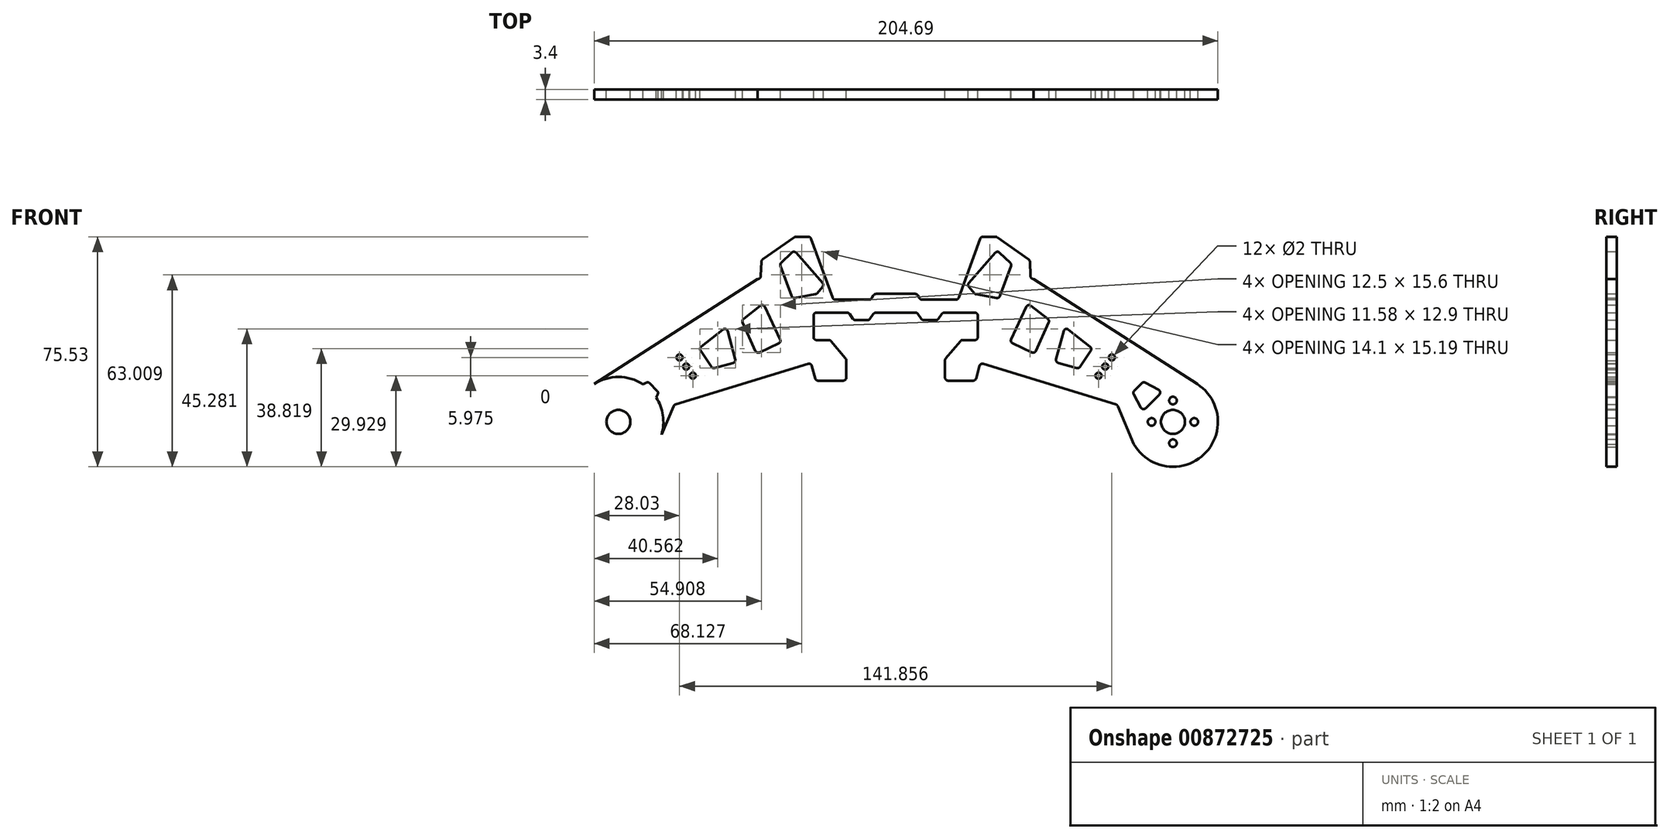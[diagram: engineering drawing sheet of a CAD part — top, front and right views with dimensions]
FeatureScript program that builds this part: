
annotation { "Feature Type Name" : "Feature", "Feature Type Description" : "" }
export const myFeature = defineFeature(function(context is Context, id is Id, definition is map)
    precondition{}
    {
        {
            var Q0;
            Q0=qCreatedBy(makeId("Front.planeOp"),FACE);
            var sketch = newSketch(context, id + "F0", { "sketchPlane" : qUnion([Q0])});
            skLineSegment(sketch, "E0", {"start": v(-61.98, 49.43) * mm, "end": v(-8.3, 14.94) * mm});
            skCircle(sketch, "E1", {"center": v(-16.27, 2.53) * mm, "radius": 14.75 * mm});
            skLineSegment(sketch, "E2", {"start": v(-35, 8.26) * mm, "end": v(-78.52, 21.56) * mm});
            skLineSegment(sketch, "E3", {"start": v(-63, 50.39) * mm, "end": v(-63.19, 55.07) * mm});
            skLineSegment(sketch, "E4", {"start": v(-63.61, 55.85) * mm, "end": v(-74, 63.13) * mm});
            skLineSegment(sketch, "E5", {"start": v(-74.58, 63.31) * mm, "end": v(-78.56, 63.31) * mm});
            skLineSegment(sketch, "E6", {"start": v(-79.5, 62.65) * mm, "end": v(-86.55, 43.3) * mm});
            skLineSegment(sketch, "E7", {"start": v(-87.49, 42.64) * mm, "end": v(-98.58, 42.64) * mm});
            skLineSegment(sketch, "E8", {"start": v(-99.44, 43.14) * mm, "end": v(-99.96, 44.04) * mm});
            skLineSegment(sketch, "E9", {"start": v(-100.83, 44.54) * mm, "end": v(-107.25, 44.54) * mm});
            skLineSegment(sketch, "E10", {"start": v(-79.77, 20.86) * mm, "end": v(-80.86, 16.81) * mm});
            skLineSegment(sketch, "E11", {"start": v(-81.83, 16.07) * mm, "end": v(-90.06, 16.07) * mm});
            skLineSegment(sketch, "E12", {"start": v(-91.06, 17.07) * mm, "end": v(-91.06, 22.7) * mm});
            skLineSegment(sketch, "E13", {"start": v(-90.83, 23.35) * mm, "end": v(-86.06, 29.03) * mm});
            skLineSegment(sketch, "E14", {"start": v(-85.3, 29.39) * mm, "end": v(-81.3, 29.39) * mm});
            skLineSegment(sketch, "E15", {"start": v(-80.3, 30.39) * mm, "end": v(-80.3, 37.39) * mm});
            skLineSegment(sketch, "E16", {"start": v(-81.3, 38.39) * mm, "end": v(-91.3, 38.39) * mm});
            skLineSegment(sketch, "E17", {"start": v(-92.1, 37.96) * mm, "end": v(-93.23, 36.36) * mm});
            skLineSegment(sketch, "E18", {"start": v(-94.05, 35.93) * mm, "end": v(-98.01, 35.93) * mm});
            skLineSegment(sketch, "E19", {"start": v(-98.83, 36.36) * mm, "end": v(-99.95, 37.96) * mm});
            skLineSegment(sketch, "E20", {"start": v(-100.77, 38.39) * mm, "end": v(-107.25, 38.39) * mm});
            skLineSegment(sketch, "E21", {"start": v(-34.38, 7.7) * mm, "end": v(-29.1, -4.76) * mm});
            skCircle(sketch, "E22", {"center": v(-16.27, 2.53) * mm, "radius": 3.93 * mm});
            skLineSegment(sketch, "E23", {"start": v(-16.27, 2.53) * mm, "end": v(-16.27, 9.53) * mm, "construction": true});
            skLineSegment(sketch, "E24", {"start": v(-16.27, 2.53) * mm, "end": v(-9.27, 2.53) * mm, "construction": true});
            skLineSegment(sketch, "E25", {"start": v(-16.27, 2.53) * mm, "end": v(-23.27, 2.53) * mm, "construction": true});
            skLineSegment(sketch, "E26", {"start": v(-16.27, 2.53) * mm, "end": v(-16.27, -4.47) * mm, "construction": true});
            skCircle(sketch, "E27", {"center": v(-16.27, -4.47) * mm, "radius": 1.25 * mm});
            skCircle(sketch, "E28", {"center": v(-9.27, 2.53) * mm, "radius": 1.25 * mm});
            skCircle(sketch, "E29", {"center": v(-16.27, 9.53) * mm, "radius": 1.25 * mm});
            skCircle(sketch, "E30", {"center": v(-23.27, 2.53) * mm, "radius": 1.25 * mm});
            skLineSegment(sketch, "E31", {"start": v(-25.22, 7.02) * mm, "end": v(-20.75, 11.48) * mm});
            skLineSegment(sketch, "E32", {"start": v(-20.99, 13.07) * mm, "end": v(-25.3, 15.4) * mm});
            skLineSegment(sketch, "E33", {"start": v(-26.5, 15.23) * mm, "end": v(-28.97, 12.75) * mm});
            skLineSegment(sketch, "E34", {"start": v(-29.14, 11.57) * mm, "end": v(-26.8, 7.25) * mm});
            skPoint(sketch, "E35", {"position": v(-22.99, 9.25) * mm});
            skCircle(sketch, "E36", {"center": v(-40.68, 17.7) * mm, "radius": 1 * mm});
            skCircle(sketch, "E37", {"center": v(-38.5, 20.7) * mm, "radius": 1 * mm});
            skCircle(sketch, "E38", {"center": v(-36.32, 23.68) * mm, "radius": 1 * mm});
            skLineSegment(sketch, "E39", {"start": v(-38.5, 20.7) * mm, "end": v(-40.68, 17.7) * mm, "construction": true});
            skLineSegment(sketch, "E40", {"start": v(-36.32, 23.68) * mm, "end": v(-38.5, 20.7) * mm, "construction": true});
            skLineSegment(sketch, "E41", {"start": v(-46.77, 20.6) * mm, "end": v(-43.24, 25.86) * mm});
            skLineSegment(sketch, "E42", {"start": v(-43.45, 27.2) * mm, "end": v(-50.54, 32.83) * mm});
            skLineSegment(sketch, "E43", {"start": v(-52.13, 32.31) * mm, "end": v(-54.61, 23.14) * mm});
            skLineSegment(sketch, "E44", {"start": v(-53.92, 21.92) * mm, "end": v(-47.88, 20.19) * mm});
            skPoint(sketch, "E45", {"position": v(-44.95, 23.3) * mm});
            skPoint(sketch, "E46.endSnap0", {"position": v(-57.03, 15) * mm});
            skLineSegment(sketch, "E47", {"start": v(-62.54, 25.36) * mm, "end": v(-68.87, 28.3) * mm});
            skLineSegment(sketch, "E48", {"start": v(-69.36, 29.64) * mm, "end": v(-64.4, 40.28) * mm});
            skLineSegment(sketch, "E49", {"start": v(-62.87, 40.65) * mm, "end": v(-57.34, 36.36) * mm});
            skLineSegment(sketch, "E50", {"start": v(-57.04, 35.16) * mm, "end": v(-61.2, 25.85) * mm});
            skPoint(sketch, "E51.visualSharp", {"position": v(-63.86, 41.42) * mm});
            skArc(sketch, "E51.filletArc", {"start": v(-62.87, 40.65) * mm, "mid": v(-63.72, 40.83) * mm, "end": v(-64.4, 40.28) * mm});
            skPoint(sketch, "E52.visualSharp", {"position": v(-56.72, 35.88) * mm});
            skArc(sketch, "E52.filletArc", {"start": v(-57.04, 35.16) * mm, "mid": v(-56.98, 35.81) * mm, "end": v(-57.34, 36.36) * mm});
            skPoint(sketch, "E53.visualSharp", {"position": v(-69.78, 28.73) * mm});
            skArc(sketch, "E53.filletArc", {"start": v(-69.36, 29.64) * mm, "mid": v(-69.4, 28.87) * mm, "end": v(-68.87, 28.3) * mm});
            skPoint(sketch, "E54.visualSharp", {"position": v(-61.62, 24.93) * mm});
            skArc(sketch, "E54.filletArc", {"start": v(-62.54, 25.36) * mm, "mid": v(-61.77, 25.32) * mm, "end": v(-61.2, 25.85) * mm});
            skPoint(sketch, "E55.visualSharp", {"position": v(-51.73, 33.78) * mm});
            skArc(sketch, "E55.filletArc", {"start": v(-50.54, 32.83) * mm, "mid": v(-51.48, 33) * mm, "end": v(-52.13, 32.31) * mm});
            skPoint(sketch, "E56.visualSharp", {"position": v(-42.72, 26.63) * mm});
            skArc(sketch, "E56.filletArc", {"start": v(-43.24, 25.86) * mm, "mid": v(-43.08, 26.58) * mm, "end": v(-43.45, 27.2) * mm});
            skPoint(sketch, "E57.visualSharp", {"position": v(-54.87, 22.2) * mm});
            skArc(sketch, "E57.filletArc", {"start": v(-54.61, 23.14) * mm, "mid": v(-54.52, 22.4) * mm, "end": v(-53.92, 21.92) * mm});
            skPoint(sketch, "E58.visualSharp", {"position": v(-47.18, 19.99) * mm});
            skArc(sketch, "E58.filletArc", {"start": v(-47.88, 20.19) * mm, "mid": v(-47.26, 20.21) * mm, "end": v(-46.77, 20.6) * mm});
            skPoint(sketch, "E59.visualSharp", {"position": v(-29.5, 12.22) * mm});
            skArc(sketch, "E59.filletArc", {"start": v(-28.97, 12.75) * mm, "mid": v(-29.25, 12.19) * mm, "end": v(-29.14, 11.57) * mm});
            skPoint(sketch, "E60.visualSharp", {"position": v(-25.96, 15.76) * mm});
            skArc(sketch, "E60.filletArc", {"start": v(-25.3, 15.4) * mm, "mid": v(-25.93, 15.52) * mm, "end": v(-26.5, 15.23) * mm});
            skPoint(sketch, "E61.visualSharp", {"position": v(-26.17, 6.07) * mm});
            skArc(sketch, "E61.filletArc", {"start": v(-26.8, 7.25) * mm, "mid": v(-26.07, 6.73) * mm, "end": v(-25.22, 7.02) * mm});
            skPoint(sketch, "E62.visualSharp", {"position": v(-19.8, 12.43) * mm});
            skArc(sketch, "E62.filletArc", {"start": v(-20.75, 11.48) * mm, "mid": v(-20.47, 12.33) * mm, "end": v(-20.99, 13.07) * mm});
            skPoint(sketch, "E63.visualSharp", {"position": v(-62.99, 50.07) * mm});
            skArc(sketch, "E63.filletArc", {"start": v(-63, 50.39) * mm, "mid": v(-62.68, 49.7) * mm, "end": v(-61.98, 49.43) * mm});
            skPoint(sketch, "E64.visualSharp", {"position": v(-63.2, 55.57) * mm});
            skArc(sketch, "E64.filletArc", {"start": v(-63.19, 55.07) * mm, "mid": v(-63.3, 55.51) * mm, "end": v(-63.61, 55.85) * mm});
            skPoint(sketch, "E65.visualSharp", {"position": v(-100.25, 38.39) * mm});
            skArc(sketch, "E65.filletArc", {"start": v(-99.95, 37.96) * mm, "mid": v(-100.31, 38.28) * mm, "end": v(-100.77, 38.39) * mm});
            skPoint(sketch, "E66.visualSharp", {"position": v(-98.53, 35.93) * mm});
            skArc(sketch, "E66.filletArc", {"start": v(-98.83, 36.36) * mm, "mid": v(-98.47, 36.04) * mm, "end": v(-98.01, 35.93) * mm});
            skPoint(sketch, "E67.visualSharp", {"position": v(-93.53, 35.93) * mm});
            skArc(sketch, "E67.filletArc", {"start": v(-94.05, 35.93) * mm, "mid": v(-93.6, 36.04) * mm, "end": v(-93.23, 36.36) * mm});
            skPoint(sketch, "E68.visualSharp", {"position": v(-91.81, 38.39) * mm});
            skArc(sketch, "E68.filletArc", {"start": v(-91.3, 38.39) * mm, "mid": v(-91.75, 38.28) * mm, "end": v(-92.1, 37.96) * mm});
            skPoint(sketch, "E69.visualSharp", {"position": v(-80.3, 38.39) * mm});
            skArc(sketch, "E69.filletArc", {"start": v(-80.3, 37.39) * mm, "mid": v(-80.58, 38.1) * mm, "end": v(-81.3, 38.39) * mm});
            skPoint(sketch, "E70.visualSharp", {"position": v(-80.3, 29.39) * mm});
            skArc(sketch, "E70.filletArc", {"start": v(-81.3, 29.39) * mm, "mid": v(-80.58, 29.68) * mm, "end": v(-80.3, 30.39) * mm});
            skPoint(sketch, "E71.visualSharp", {"position": v(-85.76, 29.39) * mm});
            skArc(sketch, "E71.filletArc", {"start": v(-85.3, 29.39) * mm, "mid": v(-85.71, 29.3) * mm, "end": v(-86.06, 29.03) * mm});
            skPoint(sketch, "E72.visualSharp", {"position": v(-91.06, 23.07) * mm});
            skArc(sketch, "E72.filletArc", {"start": v(-90.83, 23.35) * mm, "mid": v(-91, 23.05) * mm, "end": v(-91.06, 22.7) * mm});
            skPoint(sketch, "E73.visualSharp", {"position": v(-91.06, 16.07) * mm});
            skArc(sketch, "E73.filletArc", {"start": v(-91.06, 17.07) * mm, "mid": v(-90.77, 16.36) * mm, "end": v(-90.06, 16.07) * mm});
            skPoint(sketch, "E74.visualSharp", {"position": v(-81.06, 16.07) * mm});
            skArc(sketch, "E74.filletArc", {"start": v(-81.83, 16.07) * mm, "mid": v(-81.22, 16.28) * mm, "end": v(-80.86, 16.81) * mm});
            skPoint(sketch, "E75.visualSharp", {"position": v(-79.5, 21.87) * mm});
            skArc(sketch, "E75.filletArc", {"start": v(-78.52, 21.56) * mm, "mid": v(-79.3, 21.48) * mm, "end": v(-79.77, 20.86) * mm});
            skPoint(sketch, "E76.visualSharp", {"position": v(-86.79, 42.64) * mm});
            skArc(sketch, "E76.filletArc", {"start": v(-87.49, 42.64) * mm, "mid": v(-86.91, 42.82) * mm, "end": v(-86.55, 43.3) * mm});
            skPoint(sketch, "E77.visualSharp", {"position": v(-34.56, 8.12) * mm});
            skArc(sketch, "E77.filletArc", {"start": v(-34.38, 7.7) * mm, "mid": v(-34.63, 8.05) * mm, "end": v(-35, 8.26) * mm});
            skPoint(sketch, "E78.visualSharp", {"position": v(-79.26, 63.31) * mm});
            skArc(sketch, "E78.filletArc", {"start": v(-78.56, 63.31) * mm, "mid": v(-79.14, 63.13) * mm, "end": v(-79.5, 62.65) * mm});
            skPoint(sketch, "E79.visualSharp", {"position": v(-74.26, 63.31) * mm});
            skArc(sketch, "E79.filletArc", {"start": v(-74, 63.13) * mm, "mid": v(-74.28, 63.27) * mm, "end": v(-74.58, 63.31) * mm});
            skLineSegment(sketch, "E80.MirrorCS", {"start": v(-74.58, 58.04) * mm, "end": v(-83.22, 48.2) * mm});
            skLineSegment(sketch, "E81.MirrorCS", {"start": v(-69.68, 54.77) * mm, "end": v(-73.13, 58.1) * mm});
            skLineSegment(sketch, "E82.MirrorCS", {"start": v(-80.87, 44.42) * mm, "end": v(-74.18, 43.21) * mm});
            skLineSegment(sketch, "E83.MirrorCS", {"start": v(-73.07, 43.85) * mm, "end": v(-69.43, 53.7) * mm});
            skLineSegment(sketch, "E84.MirrorCS", {"start": v(-83.24, 46.9) * mm, "end": v(-81.46, 44.77) * mm});
            skPoint(sketch, "E85.MirrorP", {"position": v(-86.1, 45.52) * mm});
            skPoint(sketch, "E86.visualSharp", {"position": v(-73.89, 58.83) * mm});
            skArc(sketch, "E86.filletArc", {"start": v(-73.13, 58.1) * mm, "mid": v(-73.87, 58.38) * mm, "end": v(-74.58, 58.04) * mm});
            skPoint(sketch, "E87.visualSharp", {"position": v(-69.2, 54.32) * mm});
            skArc(sketch, "E87.filletArc", {"start": v(-69.43, 53.7) * mm, "mid": v(-69.4, 54.28) * mm, "end": v(-69.68, 54.77) * mm});
            skPoint(sketch, "E88.visualSharp", {"position": v(-73.36, 43.06) * mm});
            skArc(sketch, "E88.filletArc", {"start": v(-74.18, 43.21) * mm, "mid": v(-73.5, 43.33) * mm, "end": v(-73.07, 43.85) * mm});
            skPoint(sketch, "E89.visualSharp", {"position": v(-81.23, 44.49) * mm});
            skArc(sketch, "E89.filletArc", {"start": v(-81.46, 44.77) * mm, "mid": v(-81.2, 44.54) * mm, "end": v(-80.87, 44.42) * mm});
            skPoint(sketch, "E90.visualSharp", {"position": v(-83.79, 47.56) * mm});
            skArc(sketch, "E90.filletArc", {"start": v(-83.22, 48.2) * mm, "mid": v(-83.47, 47.56) * mm, "end": v(-83.24, 46.9) * mm});
            skLineSegment(sketch, "E91", {"start": v(-36.32, 23.68) * mm, "end": v(-31.73, 30) * mm, "construction": true});
            skLineSegment(sketch, "E92", {"start": v(-40.68, 17.7) * mm, "end": v(-45.28, 11.4) * mm, "construction": true});
            skLineSegment(sketch, "E93", {"start": v(-16.27, 2.53) * mm, "end": v(-22.99, 9.25) * mm, "construction": true});
            skLineSegment(sketch, "E94", {"start": v(-47.18, 19.99) * mm, "end": v(-51.64, 13.34) * mm, "construction": true});
            skPoint(sketch, "E95.endSnap0", {"position": v(-35.14, 32.18) * mm});
            skLineSegment(sketch, "E96", {"start": v(-64.55, 26.29) * mm, "end": v(-67.4, 18.16) * mm, "construction": true});
            skLineSegment(sketch, "E97", {"start": v(-54.87, 22.2) * mm, "end": v(-56.82, 15) * mm, "construction": true});
            skLineSegment(sketch, "E98", {"start": v(-42.72, 26.63) * mm, "end": v(-37.84, 33.92) * mm, "construction": true});
            skLineSegment(sketch, "E99", {"start": v(-51.73, 33.78) * mm, "end": v(-49.64, 41.5) * mm, "construction": true});
            skPoint(sketch, "E100.visualSharp", {"position": v(-100.25, 44.54) * mm});
            skArc(sketch, "E100.filletArc", {"start": v(-99.96, 44.04) * mm, "mid": v(-100.33, 44.4) * mm, "end": v(-100.83, 44.54) * mm});
            skPoint(sketch, "E101.visualSharp", {"position": v(-99.16, 42.64) * mm});
            skArc(sketch, "E101.filletArc", {"start": v(-99.44, 43.14) * mm, "mid": v(-99.08, 42.77) * mm, "end": v(-98.58, 42.64) * mm});
            skLineSegment(sketch, "E102.MirrorCS", {"start": v(-180.13, 7.7) * mm, "end": v(-185.41, -4.76) * mm});
            skCircle(sketch, "E103.MirrorC", {"center": v(-198.23, 2.53) * mm, "radius": 3.93 * mm});
            skLineSegment(sketch, "E104.MirrorCS", {"start": v(-198.23, 2.53) * mm, "end": v(-198.23, -4.47) * mm, "construction": true});
            skCircle(sketch, "E105.MirrorC", {"center": v(-198.23, 2.53) * mm, "radius": 14.75 * mm});
            skArc(sketch, "E106.MirrorCS", {"start": v(-120.45, 35.93) * mm, "mid": v(-120.91, 36.04) * mm, "end": v(-121.27, 36.36) * mm});
            skLineSegment(sketch, "E107.MirrorCS", {"start": v(-122.4, 37.96) * mm, "end": v(-121.27, 36.36) * mm});
            skArc(sketch, "E108.MirrorCS", {"start": v(-123.21, 38.39) * mm, "mid": v(-122.75, 38.28) * mm, "end": v(-122.4, 37.96) * mm});
            skArc(sketch, "E109.MirrorCS", {"start": v(-180.13, 7.7) * mm, "mid": v(-179.88, 8.05) * mm, "end": v(-179.5, 8.26) * mm});
            skArc(sketch, "E110.MirrorCS", {"start": v(-140.5, 63.13) * mm, "mid": v(-140.23, 63.27) * mm, "end": v(-139.93, 63.31) * mm});
            skArc(sketch, "E111.MirrorCS", {"start": v(-115.06, 43.14) * mm, "mid": v(-115.43, 42.77) * mm, "end": v(-115.93, 42.64) * mm});
            skLineSegment(sketch, "E112.MirrorCS", {"start": v(-178.18, 23.68) * mm, "end": v(-176, 20.7) * mm, "construction": true});
            skCircle(sketch, "E113.MirrorC", {"center": v(-178.18, 23.68) * mm, "radius": 1 * mm});
            skLineSegment(sketch, "E114.MirrorCS", {"start": v(-188.01, 15.23) * mm, "end": v(-185.53, 12.75) * mm});
            skArc(sketch, "E115.MirrorCS", {"start": v(-114.55, 37.96) * mm, "mid": v(-114.2, 38.28) * mm, "end": v(-113.73, 38.39) * mm});
            skArc(sketch, "E116.MirrorCS", {"start": v(-133.21, 29.39) * mm, "mid": v(-133.92, 29.68) * mm, "end": v(-134.21, 30.39) * mm});
            skArc(sketch, "E117.MirrorCS", {"start": v(-133.04, 44.77) * mm, "mid": v(-133.3, 44.54) * mm, "end": v(-133.63, 44.42) * mm});
            skArc(sketch, "E118.MirrorCS", {"start": v(-193.75, 11.48) * mm, "mid": v(-194.03, 12.33) * mm, "end": v(-193.52, 13.07) * mm});
            skLineSegment(sketch, "E119.MirrorCS", {"start": v(-131.26, 46.9) * mm, "end": v(-133.04, 44.77) * mm});
            skArc(sketch, "E120.MirrorCS", {"start": v(-135.99, 21.56) * mm, "mid": v(-135.21, 21.48) * mm, "end": v(-134.73, 20.86) * mm});
            skLineSegment(sketch, "E121.MirrorCS", {"start": v(-176, 20.7) * mm, "end": v(-173.82, 17.7) * mm, "construction": true});
            skLineSegment(sketch, "E122.MirrorCS", {"start": v(-115.67, 36.36) * mm, "end": v(-114.55, 37.96) * mm});
            skArc(sketch, "E123.MirrorCS", {"start": v(-151.63, 40.65) * mm, "mid": v(-150.78, 40.83) * mm, "end": v(-150.11, 40.28) * mm});
            skArc(sketch, "E124.MirrorCS", {"start": v(-145.07, 53.7) * mm, "mid": v(-145.1, 54.28) * mm, "end": v(-144.83, 54.77) * mm});
            skCircle(sketch, "E125.MirrorC", {"center": v(-173.82, 17.7) * mm, "radius": 1 * mm});
            skLineSegment(sketch, "E126.MirrorCS", {"start": v(-129.21, 29.39) * mm, "end": v(-133.21, 29.39) * mm});
            skCircle(sketch, "E127.MirrorC", {"center": v(-176, 20.7) * mm, "radius": 1 * mm});
            skArc(sketch, "E128.MirrorCS", {"start": v(-115.67, 36.36) * mm, "mid": v(-116.03, 36.04) * mm, "end": v(-116.5, 35.93) * mm});
            skArc(sketch, "E129.MirrorCS", {"start": v(-123.68, 23.35) * mm, "mid": v(-123.5, 23.05) * mm, "end": v(-123.44, 22.7) * mm});
            skLineSegment(sketch, "E130.MirrorCS", {"start": v(-115.06, 43.14) * mm, "end": v(-114.54, 44.04) * mm});
            skArc(sketch, "E131.MirrorCS", {"start": v(-127.02, 42.64) * mm, "mid": v(-127.59, 42.82) * mm, "end": v(-127.96, 43.3) * mm});
            skArc(sketch, "E132.MirrorCS", {"start": v(-132.68, 16.07) * mm, "mid": v(-133.29, 16.28) * mm, "end": v(-133.64, 16.81) * mm});
            skArc(sketch, "E133.MirrorCS", {"start": v(-131.28, 48.2) * mm, "mid": v(-131.03, 47.56) * mm, "end": v(-131.26, 46.9) * mm});
            skLineSegment(sketch, "E134.MirrorCS", {"start": v(-134.73, 20.86) * mm, "end": v(-133.64, 16.81) * mm});
            skLineSegment(sketch, "E135.MirrorCS", {"start": v(-120.45, 35.93) * mm, "end": v(-116.5, 35.93) * mm});
            skArc(sketch, "E136.MirrorCS", {"start": v(-189.2, 15.4) * mm, "mid": v(-188.58, 15.52) * mm, "end": v(-188.01, 15.23) * mm});
            skArc(sketch, "E137.MirrorCS", {"start": v(-151.32, 55.07) * mm, "mid": v(-151.2, 55.51) * mm, "end": v(-150.9, 55.85) * mm});
            skArc(sketch, "E138.MirrorCS", {"start": v(-129.21, 29.39) * mm, "mid": v(-128.8, 29.3) * mm, "end": v(-128.45, 29.03) * mm});
            skArc(sketch, "E139.MirrorCS", {"start": v(-114.54, 44.04) * mm, "mid": v(-114.17, 44.4) * mm, "end": v(-113.67, 44.54) * mm});
            skLineSegment(sketch, "E140.MirrorCS", {"start": v(-144.83, 54.77) * mm, "end": v(-141.37, 58.1) * mm});
            skArc(sketch, "E141.MirrorCS", {"start": v(-166.63, 20.19) * mm, "mid": v(-167.24, 20.21) * mm, "end": v(-167.73, 20.6) * mm});
            skArc(sketch, "E142.MirrorCS", {"start": v(-141.37, 58.1) * mm, "mid": v(-140.64, 58.38) * mm, "end": v(-139.93, 58.04) * mm});
            skArc(sketch, "E143.MirrorCS", {"start": v(-185.53, 12.75) * mm, "mid": v(-185.25, 12.19) * mm, "end": v(-185.36, 11.57) * mm});
            skLineSegment(sketch, "E144.MirrorCS", {"start": v(-113.73, 38.39) * mm, "end": v(-107.25, 38.39) * mm});
            skCircle(sketch, "E145.MirrorC", {"center": v(-198.23, -4.47) * mm, "radius": 1.25 * mm});
            skCircle(sketch, "E146.MirrorC", {"center": v(-198.23, 9.53) * mm, "radius": 1.25 * mm});
            skArc(sketch, "E147.MirrorCS", {"start": v(-145.15, 29.64) * mm, "mid": v(-145.11, 28.87) * mm, "end": v(-145.63, 28.3) * mm});
            skArc(sketch, "E148.MirrorCS", {"start": v(-134.21, 37.39) * mm, "mid": v(-133.92, 38.1) * mm, "end": v(-133.21, 38.39) * mm});
            skArc(sketch, "E149.MirrorCS", {"start": v(-157.47, 35.16) * mm, "mid": v(-157.52, 35.81) * mm, "end": v(-157.17, 36.36) * mm});
            skArc(sketch, "E150.MirrorCS", {"start": v(-163.96, 32.83) * mm, "mid": v(-163.03, 33) * mm, "end": v(-162.37, 32.31) * mm});
            skArc(sketch, "E151.MirrorCS", {"start": v(-171.27, 25.86) * mm, "mid": v(-171.42, 26.58) * mm, "end": v(-171.06, 27.2) * mm});
            skLineSegment(sketch, "E152.MirrorCS", {"start": v(-113.67, 44.54) * mm, "end": v(-107.25, 44.54) * mm});
            skLineSegment(sketch, "E153.MirrorCS", {"start": v(-193.52, 13.07) * mm, "end": v(-189.2, 15.4) * mm});
            skCircle(sketch, "E154.MirrorC", {"center": v(-205.23, 2.53) * mm, "radius": 1.25 * mm});
            skArc(sketch, "E155.MirrorCS", {"start": v(-187.7, 7.25) * mm, "mid": v(-188.43, 6.73) * mm, "end": v(-189.28, 7.02) * mm});
            skArc(sketch, "E156.MirrorCS", {"start": v(-123.44, 17.07) * mm, "mid": v(-123.74, 16.36) * mm, "end": v(-124.44, 16.07) * mm});
            skLineSegment(sketch, "E157.MirrorCS", {"start": v(-167.73, 20.6) * mm, "end": v(-171.27, 25.86) * mm});
            skArc(sketch, "E158.MirrorCS", {"start": v(-140.32, 43.21) * mm, "mid": v(-141, 43.33) * mm, "end": v(-141.44, 43.85) * mm});
            skCircle(sketch, "E159.MirrorC", {"center": v(-191.23, 2.53) * mm, "radius": 1.25 * mm});
            skLineSegment(sketch, "E160.MirrorCS", {"start": v(-139.93, 63.31) * mm, "end": v(-135.94, 63.31) * mm});
            skArc(sketch, "E161.MirrorCS", {"start": v(-135.94, 63.31) * mm, "mid": v(-135.37, 63.13) * mm, "end": v(-135, 62.65) * mm});
            skArc(sketch, "E162.MirrorCS", {"start": v(-159.9, 23.14) * mm, "mid": v(-159.99, 22.4) * mm, "end": v(-160.58, 21.92) * mm});
            skLineSegment(sketch, "E163.MirrorCS", {"start": v(-185.36, 11.57) * mm, "end": v(-187.7, 7.25) * mm});
            skLineSegment(sketch, "E164.MirrorCS", {"start": v(-189.28, 7.02) * mm, "end": v(-193.75, 11.48) * mm});
            skArc(sketch, "E165.MirrorCS", {"start": v(-151.96, 25.36) * mm, "mid": v(-152.73, 25.32) * mm, "end": v(-153.3, 25.85) * mm});
            skLineSegment(sketch, "E166.MirrorCS", {"start": v(-151.5, 50.39) * mm, "end": v(-151.32, 55.07) * mm});
            skArc(sketch, "E167.MirrorCS", {"start": v(-151.5, 50.39) * mm, "mid": v(-151.82, 49.7) * mm, "end": v(-152.53, 49.43) * mm});
            skPoint(sketch, "E168.MirrorP", {"position": v(-135, 21.87) * mm});
            skPoint(sketch, "E169.MirrorP", {"position": v(-114.25, 38.39) * mm});
            skPoint(sketch, "E170.MirrorP", {"position": v(-128.4, 45.52) * mm});
            skPoint(sketch, "E171.MirrorP", {"position": v(-140.62, 58.83) * mm});
            skLineSegment(sketch, "E172.MirrorCS", {"start": v(-160.58, 21.92) * mm, "end": v(-166.63, 20.19) * mm});
            skLineSegment(sketch, "E173.MirrorCS", {"start": v(-151.96, 25.36) * mm, "end": v(-145.63, 28.3) * mm});
            skLineSegment(sketch, "E174.MirrorCS", {"start": v(-141.44, 43.85) * mm, "end": v(-145.07, 53.7) * mm});
            skLineSegment(sketch, "E175.MirrorCS", {"start": v(-134.21, 30.39) * mm, "end": v(-134.21, 37.39) * mm});
            skLineSegment(sketch, "E176.MirrorCS", {"start": v(-198.23, 2.53) * mm, "end": v(-191.23, 2.53) * mm, "construction": true});
            skPoint(sketch, "E177.MirrorP", {"position": v(-114.25, 44.54) * mm});
            skPoint(sketch, "E178.MirrorP", {"position": v(-152.88, 24.93) * mm});
            skLineSegment(sketch, "E179.MirrorCS", {"start": v(-133.21, 38.39) * mm, "end": v(-123.21, 38.39) * mm});
            skLineSegment(sketch, "E180.MirrorCS", {"start": v(-139.93, 58.04) * mm, "end": v(-131.28, 48.2) * mm});
            skLineSegment(sketch, "E181.MirrorCS", {"start": v(-150.9, 55.85) * mm, "end": v(-140.5, 63.13) * mm});
            skLineSegment(sketch, "E182.MirrorCS", {"start": v(-171.06, 27.2) * mm, "end": v(-163.96, 32.83) * mm});
            skLineSegment(sketch, "E183.MirrorCS", {"start": v(-123.44, 17.07) * mm, "end": v(-123.44, 22.7) * mm});
            skLineSegment(sketch, "E184.MirrorCS", {"start": v(-133.63, 44.42) * mm, "end": v(-140.32, 43.21) * mm});
            skLineSegment(sketch, "E185.MirrorCS", {"start": v(-132.68, 16.07) * mm, "end": v(-124.44, 16.07) * mm});
            skPoint(sketch, "E186.MirrorP", {"position": v(-130.72, 47.56) * mm});
            skPoint(sketch, "E187.MirrorP", {"position": v(-120.97, 35.93) * mm});
            skPoint(sketch, "E188.MirrorP", {"position": v(-191.52, 9.25) * mm});
            skLineSegment(sketch, "E189.MirrorCS", {"start": v(-151.63, 40.65) * mm, "end": v(-157.17, 36.36) * mm});
            skPoint(sketch, "E190.MirrorP", {"position": v(-115.97, 35.93) * mm});
            skLineSegment(sketch, "E191.MirrorCS", {"start": v(-198.23, 2.53) * mm, "end": v(-191.52, 9.25) * mm, "construction": true});
            skLineSegment(sketch, "E192.MirrorCS", {"start": v(-149.96, 26.29) * mm, "end": v(-147.1, 18.16) * mm, "construction": true});
            skLineSegment(sketch, "E193.MirrorCS", {"start": v(-198.23, 2.53) * mm, "end": v(-198.23, 9.53) * mm, "construction": true});
            skPoint(sketch, "E194.MirrorP", {"position": v(-145.3, 54.32) * mm});
            skLineSegment(sketch, "E195.MirrorCS", {"start": v(-162.37, 32.31) * mm, "end": v(-159.9, 23.14) * mm});
            skLineSegment(sketch, "E196.MirrorCS", {"start": v(-159.64, 22.2) * mm, "end": v(-157.69, 15) * mm, "construction": true});
            skLineSegment(sketch, "E197.MirrorCS", {"start": v(-123.68, 23.35) * mm, "end": v(-128.45, 29.03) * mm});
            skPoint(sketch, "E198.MirrorP", {"position": v(-127.72, 42.64) * mm});
            skPoint(sketch, "E199.MirrorP", {"position": v(-162.77, 33.78) * mm});
            skLineSegment(sketch, "E200.MirrorCS", {"start": v(-152.53, 49.43) * mm, "end": v(-206.2, 14.94) * mm});
            skPoint(sketch, "E201.MirrorP", {"position": v(-157.47, 15) * mm});
            skPoint(sketch, "E202.MirrorP", {"position": v(-123.44, 16.07) * mm});
            skPoint(sketch, "E203.MirrorP", {"position": v(-179.37, 32.18) * mm});
            skLineSegment(sketch, "E204.MirrorCS", {"start": v(-179.5, 8.26) * mm, "end": v(-135.99, 21.56) * mm});
            skPoint(sketch, "E205.MirrorP", {"position": v(-141.15, 43.06) * mm});
            skPoint(sketch, "E206.MirrorP", {"position": v(-171.78, 26.63) * mm});
            skPoint(sketch, "E207.MirrorP", {"position": v(-157.79, 35.88) * mm});
            skLineSegment(sketch, "E208.MirrorCS", {"start": v(-173.82, 17.7) * mm, "end": v(-169.23, 11.4) * mm, "construction": true});
            skLineSegment(sketch, "E209.MirrorCS", {"start": v(-157.47, 35.16) * mm, "end": v(-153.3, 25.85) * mm});
            skLineSegment(sketch, "E210.MirrorCS", {"start": v(-171.78, 26.63) * mm, "end": v(-176.67, 33.92) * mm, "construction": true});
            skLineSegment(sketch, "E211.MirrorCS", {"start": v(-198.23, 2.53) * mm, "end": v(-205.23, 2.53) * mm, "construction": true});
            skPoint(sketch, "E212.MirrorP", {"position": v(-188.54, 15.76) * mm});
            skPoint(sketch, "E213.MirrorP", {"position": v(-115.35, 42.64) * mm});
            skPoint(sketch, "E214.MirrorP", {"position": v(-179.94, 8.12) * mm});
            skPoint(sketch, "E215.MirrorP", {"position": v(-140.24, 63.31) * mm});
            skPoint(sketch, "E216.MirrorP", {"position": v(-135.24, 63.31) * mm});
            skPoint(sketch, "E217.MirrorP", {"position": v(-128.75, 29.39) * mm});
            skPoint(sketch, "E218.MirrorP", {"position": v(-144.72, 28.73) * mm});
            skPoint(sketch, "E219.MirrorP", {"position": v(-194.7, 12.43) * mm});
            skPoint(sketch, "E220.MirrorP", {"position": v(-134.21, 38.39) * mm});
            skPoint(sketch, "E221.MirrorP", {"position": v(-150.64, 41.42) * mm});
            skPoint(sketch, "E222.MirrorP", {"position": v(-151.3, 55.57) * mm});
            skPoint(sketch, "E223.MirrorP", {"position": v(-185, 12.22) * mm});
            skLineSegment(sketch, "E224.MirrorCS", {"start": v(-135, 62.65) * mm, "end": v(-127.96, 43.3) * mm});
            skPoint(sketch, "E225.MirrorP", {"position": v(-159.64, 22.2) * mm});
            skPoint(sketch, "E226.MirrorP", {"position": v(-151.52, 50.07) * mm});
            skPoint(sketch, "E227.MirrorP", {"position": v(-133.27, 44.49) * mm});
            skPoint(sketch, "E228.MirrorP", {"position": v(-167.33, 19.99) * mm});
            skPoint(sketch, "E229.MirrorP", {"position": v(-123.44, 23.07) * mm});
            skLineSegment(sketch, "E230.MirrorCS", {"start": v(-162.77, 33.78) * mm, "end": v(-164.86, 41.5) * mm, "construction": true});
            skPoint(sketch, "E231.MirrorP", {"position": v(-169.55, 23.3) * mm});
            skPoint(sketch, "E232.MirrorP", {"position": v(-133.44, 16.07) * mm});
            skPoint(sketch, "E233.MirrorP", {"position": v(-122.7, 38.39) * mm});
            skLineSegment(sketch, "E234.MirrorCS", {"start": v(-178.18, 23.68) * mm, "end": v(-182.78, 30) * mm, "construction": true});
            skLineSegment(sketch, "E235.MirrorCS", {"start": v(-167.33, 19.99) * mm, "end": v(-162.87, 13.34) * mm, "construction": true});
            skPoint(sketch, "E236.MirrorP", {"position": v(-134.21, 29.39) * mm});
            skLineSegment(sketch, "E237.MirrorCS", {"start": v(-145.15, 29.64) * mm, "end": v(-150.11, 40.28) * mm});
            skLineSegment(sketch, "E238.MirrorCS", {"start": v(-127.02, 42.64) * mm, "end": v(-115.93, 42.64) * mm});
            skPoint(sketch, "E239.MirrorP", {"position": v(-188.33, 6.07) * mm});
            skSolve(sketch);
        }
        {
            var Q0;
            {var subQ6=sQuery(id+"F0.wireOp",EDGE,"E0");Q0=makeQuery(id+"F0.imprint","IMPRINT",FACE,{"disambiguationData":[TD([[makeQuery(id+"F0.imprint","IMPRINT",EDGE,{"derivedFrom":subQ6}),-1.0]])]});}
            var Q1;
            Q1=makeQuery(id+"F0.imprint","IMPRINT",FACE,{"disambiguationData":[TD([[makeQuery(id+"F0.imprint","IMPRINT",EDGE,{"derivedFrom":sQuery(id+"F0.wireOp",EDGE,"E22")}),-1.0]])]});
            var Q2;
            Q2=makeQuery(id+"F0.imprint","IMPRINT",FACE,{"disambiguationData":[TD([[makeQuery(id+"F0.imprint","IMPRINT",EDGE,{"derivedFrom":sQuery(id+"F0.wireOp",EDGE,"E2")}),-1.0]])]});
            var Q3;
            Q3=makeQuery(id+"F0.imprint","IMPRINT",FACE,{"disambiguationData":[TD([[makeQuery(id+"F0.imprint","IMPRINT",EDGE,{"derivedFrom":sQuery(id+"F0.wireOp",EDGE,"GO7SgaGN-14ix-WvzC-RXo5-p7i4nn4guVte")}),-1.0]])]});
            var Q4;
            {var subQ10=sQuery(id+"F0.wireOp",EDGE,"03afe3cf-b3bd-4cc6-bd7e-a664cd314d599.MirrorCS");Q4=makeQuery(id+"F0.imprint","IMPRINT",FACE,{"disambiguationData":[TD([[makeQuery(id+"F0.imprint","IMPRINT",EDGE,{"derivedFrom":subQ10}),1.0]])]});}
            var Q5;
            Q5=makeQuery(id+"F0.imprint","IMPRINT",FACE,{"disambiguationData":[TD([[makeQuery(id+"F0.imprint","IMPRINT",EDGE,{"derivedFrom":sQuery(id+"F0.wireOp",EDGE,"E103.MirrorC")}),1.0]])]});
            extrude(context, id + "F1", {"entities" : qUnion([Q0, Q1, Q2, Q3, Q4, Q5]), "depth" : 3.4 * mm, "offsetDistance" : 25 * mm});
        }
    });
